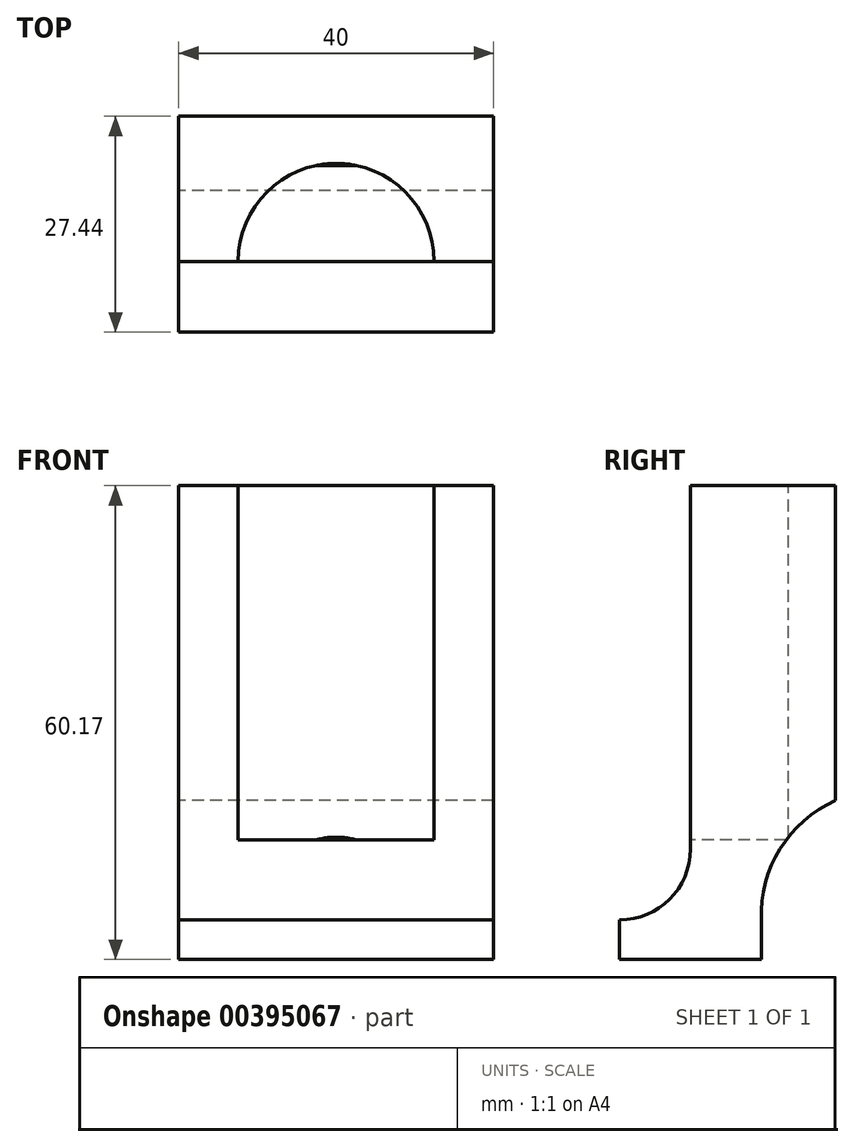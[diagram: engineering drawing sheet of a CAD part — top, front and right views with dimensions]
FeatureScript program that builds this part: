
annotation { "Feature Type Name" : "Feature", "Feature Type Description" : "" }
export const myFeature = defineFeature(function(context is Context, id is Id, definition is map)
    precondition{}
    {
        {
            var Q0;
            Q0=qCreatedBy(makeId("Right.planeOp"),FACE);
            var sketch = newSketch(context, id + "F0", { "sketchPlane" : qUnion([Q0])});
            skLineSegment(sketch, "E0", {"start": v(-9, -16.55) * mm, "end": v(9, -16.55) * mm});
            skLineSegment(sketch, "E1", {"start": v(-9, -16.55) * mm, "end": v(-9, -11.55) * mm});
            skLineSegment(sketch, "E2", {"start": v(0, 43.62) * mm, "end": v(18.44, 43.62) * mm});
            skLineSegment(sketch, "E3", {"start": v(18.44, 43.62) * mm, "end": v(18.44, 3.62) * mm});
            skLineSegment(sketch, "E4", {"start": v(0, 43.62) * mm, "end": v(0, -2.55) * mm});
            skArc(sketch, "E5", {"start": v(-9, -11.55) * mm, "mid": v(-2.64, -8.91) * mm, "end": v(0, -2.55) * mm});
            skPoint(sketch, "E6", {"position": v(0, -16.55) * mm});
            skLineSegment(sketch, "E7", {"start": v(9, -16.55) * mm, "end": v(9, -11.55) * mm});
            skArc(sketch, "E8", {"start": v(18.44, 3.62) * mm, "mid": v(11.4, -2.52) * mm, "end": v(9, -11.55) * mm});
            skSolve(sketch);
        }
        {
            var Q0;
            Q0=makeQuery(id+"F0.imprint","IMPRINT",FACE,{"disambiguationData":[TD([[makeQuery(id+"F0.imprint","IMPRINT",EDGE,{"derivedFrom":sQuery(id+"F0.wireOp",EDGE,"E0")}),1.0]])]});
            extrude(context, id + "F1", {"entities" : qUnion([Q0]), "endBound" : BoundingType.SYMMETRIC, "depth" : 40 * mm});
        }
        {
            var Q0;
            Q0=makeQuery(id+"F1.opExtrude","SWEPT_FACE",FACE,{"disambiguationData":[OSD([sQuery(id+"F0.wireOp",EDGE,"E2")])]});
            var sketch = newSketch(context, id + "F2", { "sketchPlane" : qUnion([Q0])});
            skCircle(sketch, "E9", {"center": v(0, 0) * mm, "radius": 12.44 * mm});
            skCircle(sketch, "E10.0", {"center": v(0, 0) * mm, "radius": 16.44 * mm});
            skLineSegment(sketch, "E11", {"start": v(16.44, 0) * mm, "end": v(-16.44, 0) * mm});
            skFitSpline(sketch, "E12", {"points": [v(16.44, 0) * mm, v(20, 18.44) * mm], "startDerivative": vector(0, 27.66) * mm, "endDerivative": vector(0, 27.66) * mm});
            skFitSpline(sketch, "E13", {"points": [v(-16.44, 0) * mm, v(-20, 18.44) * mm], "startDerivative": vector(0, 27.66) * mm, "endDerivative": vector(0, 27.66) * mm});
            skSolve(sketch);
        }
        {
            var Q0;
            {var subQ0=sQuery(id+"F2.wireOp",EDGE,"E11");var subQ1=sQuery(id+"F2.wireOp",EDGE,"E9");var subQ2=makeQuery(id+"F2.imprint","INTERSECT",VERTEX,{"disambiguationData":[OD(0.0)],"derivedFrom":[subQ1,subQ0]});Q0=makeQuery(id+"F2.imprint","IMPRINT",FACE,{"disambiguationData":[TD([[makeQuery(id+"F2.imprint","IMPRINT",EDGE,{"disambiguationData":[TD([[subQ2,-1.0]])],"derivedFrom":subQ1}),1.0]])]});}
            extrude(context, id + "F3", {"entities" : qUnion([Q0]), "operationType" : NewBodyOperationType.REMOVE, "oppositeDirection" : true, "depth" : 45 * mm});
        }
    });
